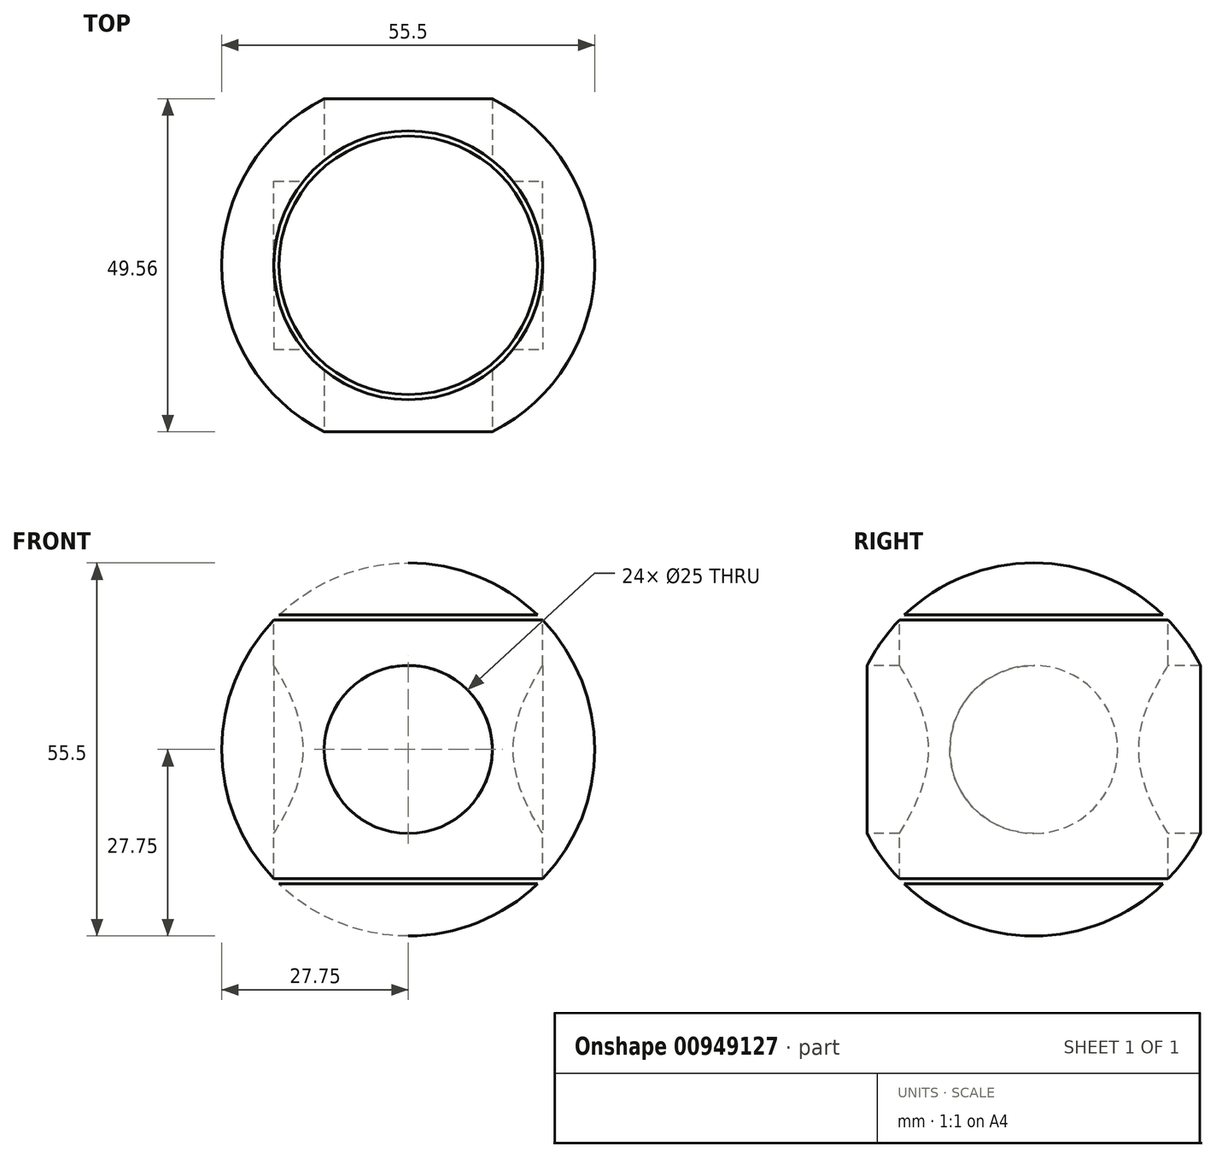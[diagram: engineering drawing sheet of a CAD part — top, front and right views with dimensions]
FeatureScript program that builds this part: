
annotation { "Feature Type Name" : "Feature", "Feature Type Description" : "" }
export const myFeature = defineFeature(function(context is Context, id is Id, definition is map)
    precondition{}
    {
        {
            var Q0;
            Q0=qCreatedBy(makeId("Front.planeOp"),FACE);
            var sketch = newSketch(context, id + "F0", { "sketchPlane" : qUnion([Q0])});
            skArc(sketch, "E0", {"start": v(0, -27.75) * mm, "mid": v(27.75, 0) * mm, "end": v(0, 27.75) * mm});
            skLineSegment(sketch, "E1", {"start": v(0, 27.75) * mm, "end": v(0, -27.75) * mm});
            skSolve(sketch);
        }
        {
            var Q0;
            Q0=makeQuery(id+"F0.imprint","IMPRINT",FACE,{"disambiguationData":[TD([[makeQuery(id+"F0.imprint","IMPRINT",EDGE,{"derivedFrom":sQuery(id+"F0.wireOp",EDGE,"E0")}),1.0]])]});
            var Q1;
            Q1=sQuery(id+"F0.wireOp",EDGE,"E1");
            revolve(context, id + "F1", {"surfaceOperationType" : NewSurfaceOperationType.NEW, "entities" : qUnion([Q0]), "axis" : qUnion([Q1]), "revolveType" : RevolveType.FULL});
        }
        {
            var Q0;
            Q0=qCreatedBy(makeId("Front.planeOp"),FACE);
            var sketch = newSketch(context, id + "F2", { "sketchPlane" : qUnion([Q0])});
            skCircle(sketch, "E2", {"center": v(0, 0) * mm, "radius": 12.5 * mm});
            skSolve(sketch);
        }
        {
            var Q0;
            Q0=makeQuery(id+"F2.imprint","IMPRINT",FACE,{"disambiguationData":[TD([[makeQuery(id+"F2.imprint","IMPRINT",EDGE,{"derivedFrom":sQuery(id+"F2.wireOp",EDGE,"E2")}),1.0]])]});
            var Q1;
            Q1=sQuery(id+"F2.wireOp",EDGE,"E2");
            extrude(context, id + "F3", {"entities" : qUnion([Q0]), "operationType" : NewBodyOperationType.REMOVE, "surfaceEntities" : qUnion([Q1]), "endBound" : BoundingType.SYMMETRIC, "oppositeDirection" : true, "depth" : 1016 * mm, "offsetDistance" : 25.4 * mm});
        }
        {
            var Q0;
            Q0=qCreatedBy(makeId("Top.planeOp"),FACE);
            var sketch = newSketch(context, id + "F4", { "sketchPlane" : qUnion([Q0])});
            skCircle(sketch, "E3", {"center": v(0, 0) * mm, "radius": 12.5 * mm});
            skSolve(sketch);
        }
        {
            var Q0;
            Q0=makeQuery(id+"F4.imprint","IMPRINT",FACE,{"disambiguationData":[TD([[makeQuery(id+"F4.imprint","IMPRINT",EDGE,{"derivedFrom":sQuery(id+"F4.wireOp",EDGE,"E3")}),1.0]])]});
            extrude(context, id + "F5", {"entities" : qUnion([Q0]), "operationType" : NewBodyOperationType.REMOVE, "endBound" : BoundingType.SYMMETRIC, "oppositeDirection" : true, "depth" : 40 * mm, "offsetDistance" : 25.4 * mm});
        }
        {
            var Q0;
            Q0=qCreatedBy(makeId("Top.planeOp"),FACE);
            var sketch = newSketch(context, id + "F6", { "sketchPlane" : qUnion([Q0])});
            skCircle(sketch, "E4", {"center": v(0, 0) * mm, "radius": 20 * mm});
            skSolve(sketch);
        }
        {
            var Q0;
            Q0=makeQuery(id+"F6.imprint","IMPRINT",FACE,{"disambiguationData":[TD([[makeQuery(id+"F6.imprint","IMPRINT",EDGE,{"derivedFrom":sQuery(id+"F6.wireOp",EDGE,"E4")}),1.0]])]});
            extrude(context, id + "F7", {"entities" : qUnion([Q0]), "operationType" : NewBodyOperationType.REMOVE, "endBound" : BoundingType.SYMMETRIC, "oppositeDirection" : true, "depth" : 40 * mm, "offsetDistance" : 25.4 * mm});
        }
        {
            var Q0;
            Q0=qCreatedBy(makeId("Right.planeOp"),FACE);
            var sketch = newSketch(context, id + "F8", { "sketchPlane" : qUnion([Q0])});
            skCircle(sketch, "E5", {"center": v(0, 0) * mm, "radius": 12.5 * mm});
            skSolve(sketch);
        }
        {
            var Q0;
            Q0=makeQuery(id+"F8.imprint","IMPRINT",FACE,{"disambiguationData":[TD([[makeQuery(id+"F8.imprint","IMPRINT",EDGE,{"derivedFrom":sQuery(id+"F8.wireOp",EDGE,"E5")}),1.0]])]});
            extrude(context, id + "F9", {"entities" : qUnion([Q0]), "operationType" : NewBodyOperationType.REMOVE, "endBound" : BoundingType.SYMMETRIC, "oppositeDirection" : true, "depth" : 40 * mm, "offsetDistance" : 25.4 * mm});
        }
    });
